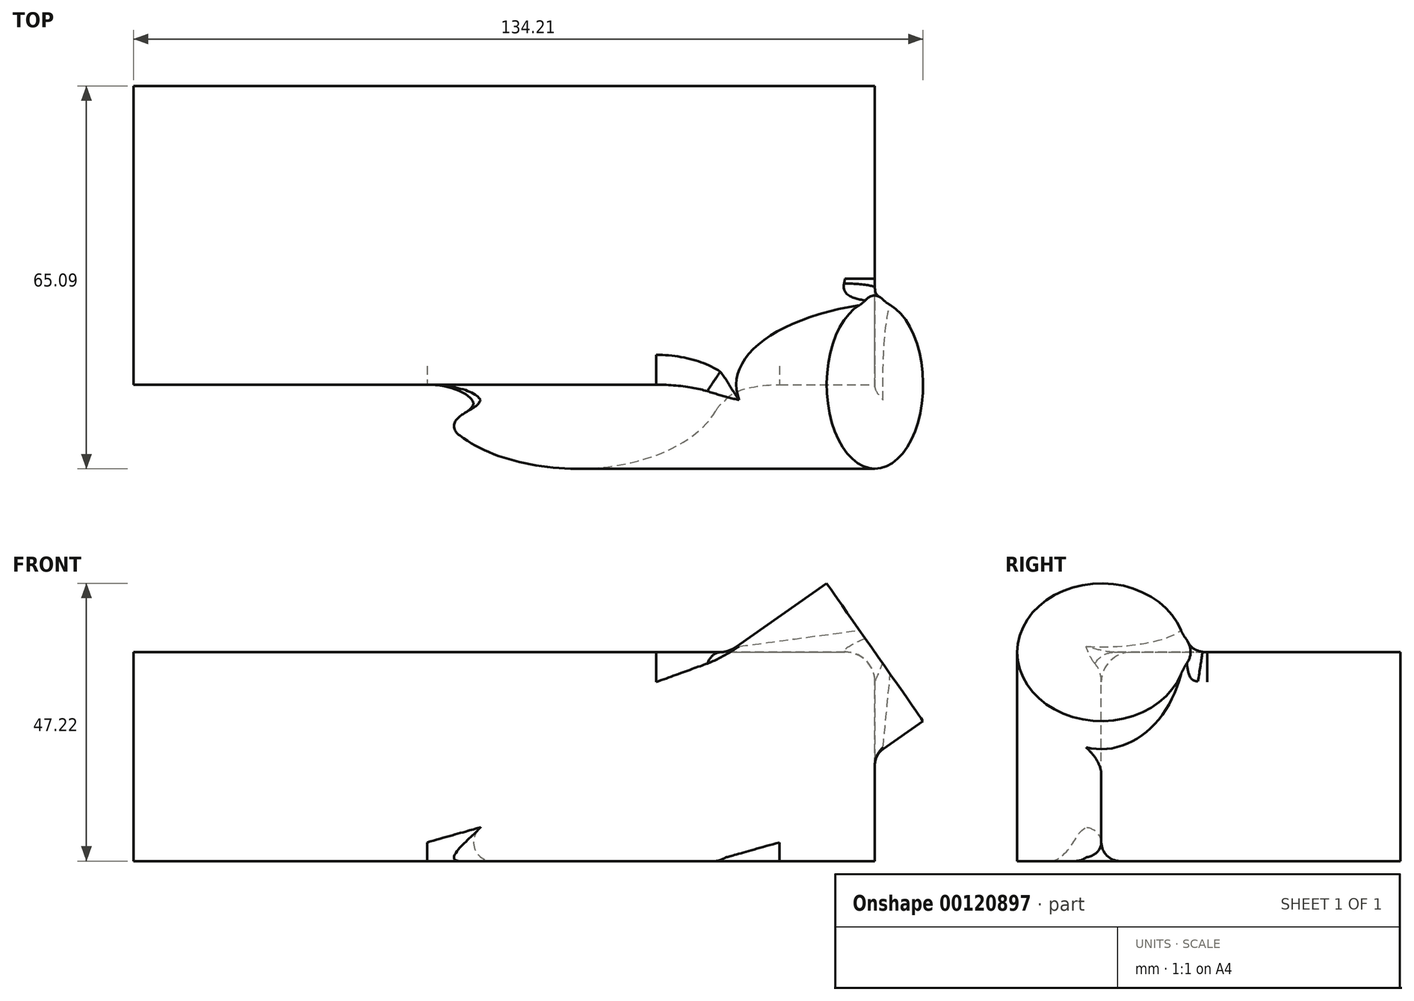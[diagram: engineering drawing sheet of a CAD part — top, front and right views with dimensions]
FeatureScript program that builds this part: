
annotation { "Feature Type Name" : "Feature", "Feature Type Description" : "" }
export const myFeature = defineFeature(function(context is Context, id is Id, definition is map)
    precondition{}
    {
        {
            var Q0;
            Q0=qCreatedBy(makeId("Front.planeOp"),FACE);
            var sketch = newSketch(context, id + "F0", { "sketchPlane" : qUnion([Q0])});
            skLineSegment(sketch, "E0.bottom", {"start": v(0, 0) * mm, "end": v(126.01, 0) * mm});
            skLineSegment(sketch, "E0.top", {"start": v(0, 35.51) * mm, "end": v(126.01, 35.51) * mm});
            skLineSegment(sketch, "E0.left", {"start": v(0, 0) * mm, "end": v(0, 35.51) * mm});
            skLineSegment(sketch, "E0.right", {"start": v(126.01, 0) * mm, "end": v(126.01, 35.51) * mm});
            skLineSegment(sketch, "E1", {"start": v(0, 0) * mm, "end": v(126.01, 35.51) * mm, "construction": true});
            skSolve(sketch);
        }
        {
            var Q0;
            Q0 = qSketchRegion(id + "F0", true);
            extrude(context, id + "F1", {"entities" : qUnion([Q0]), "endBound" : BoundingType.SYMMETRIC, "depth" : 50.8 * mm});
        }
        {
            var Q0;
            Q0=makeQuery(id+"F1.opExtrude","SWEPT_EDGE",EDGE,{"disambiguationData":[OSD([sQuery(id+"F0.wireOp",EDGE,"E0.top"),sQuery(id+"F0.wireOp",EDGE,"E0.right")])]});
            var Q1;
            Q1=makeQuery(id+"F1.opExtrude","SWEPT_FACE",FACE,{"disambiguationData":[OSD([sQuery(id+"F0.wireOp",EDGE,"E0.right")])]});
            cPlane(context, id + "F2", {"entities" : qUnion([Q0, Q1]), "cplaneType" : CPlaneType.LINE_ANGLE, "offset" : 25.4 * mm, "angle" : 325 * degree, "width" : 152.4 * mm, "height" : 152.4 * mm});
        }
        {
            var Q0;
            Q0=qCreatedBy(id+"F2.planeOp",FACE);
            var sketch = newSketch(context, id + "F3", { "sketchPlane" : qUnion([Q0])});
            skCircle(sketch, "E2", {"center": v(25.4, -43.19) * mm, "radius": 14.29 * mm});
            skSolve(sketch);
        }
        {
            var Q0;
            Q0 = qSketchRegion(id + "F3", true);
            var Q1;
            Q1=makeQuery(id+"F1.opExtrude","SWEPT_FACE",FACE,{"disambiguationData":[OSD([sQuery(id+"F0.wireOp",EDGE,"E0.bottom")])]});
            extrude(context, id + "F4", {"entities" : qUnion([Q0]), "operationType" : NewBodyOperationType.ADD, "endBound" : BoundingType.UP_TO_SURFACE, "endBoundEntityFace" : qUnion([Q1]), "depth" : 25.4 * mm});
        }
        {
            var Q0;
            Q0=makeQuery(id+"F4.boolean.opBoolean","INTERSECT",EDGE,{"disambiguationData":[OD(1.0)],"derivedFrom":[makeQuery(id+"F1.opExtrude","CAP_FACE",FACE,{"disambiguationData":[OSD([sQuery(id+"F0.wireOp",EDGE,"E0.bottom"),sQuery(id+"F0.wireOp",EDGE,"E0.top"),sQuery(id+"F0.wireOp",EDGE,"E0.left"),sQuery(id+"F0.wireOp",EDGE,"E0.right")])],"isStart":false}),makeQuery(id+"F4.opExtrude","SWEPT_FACE",FACE,{"disambiguationData":[OSD([sQuery(id+"F3.wireOp",EDGE,"E2")])]})]});
            var Q1;
            Q1=makeQuery(id+"F4.boolean.opBoolean","INTERSECT",EDGE,{"derivedFrom":[makeQuery(id+"F1.opExtrude","SWEPT_FACE",FACE,{"disambiguationData":[OSD([sQuery(id+"F0.wireOp",EDGE,"E0.right")])]}),makeQuery(id+"F4.opExtrude","SWEPT_FACE",FACE,{"disambiguationData":[OSD([sQuery(id+"F3.wireOp",EDGE,"E2")])]})]});
            var Q2;
            Q2=makeQuery(id+"F4.boolean.opBoolean","INTERSECT",EDGE,{"disambiguationData":[OD(0.0)],"derivedFrom":[makeQuery(id+"F1.opExtrude","CAP_FACE",FACE,{"disambiguationData":[OSD([sQuery(id+"F0.wireOp",EDGE,"E0.bottom"),sQuery(id+"F0.wireOp",EDGE,"E0.top"),sQuery(id+"F0.wireOp",EDGE,"E0.left"),sQuery(id+"F0.wireOp",EDGE,"E0.right")])],"isStart":false}),makeQuery(id+"F4.opExtrude","SWEPT_FACE",FACE,{"disambiguationData":[OSD([sQuery(id+"F3.wireOp",EDGE,"E2")])]})]});
            var Q3;
            {var subQ0=sQuery(id+"F0.wireOp",EDGE,"E0.bottom");var subQ1=sQuery(id+"F0.wireOp",EDGE,"E0.left");Q3=makeQuery(id+"F4.boolean.opBoolean","SPLIT",EDGE,{"disambiguationData":[TD([makeQuery(id+"F1.opExtrude","SWEPT_FACE",FACE,{"disambiguationData":[OSD([subQ1])]})])],"derivedFrom":makeQuery(id+"F1.opExtrude","CAP_EDGE",EDGE,{"disambiguationData":[OSD([subQ0])],"isStart":false})});}
            var Q4;
            {var subQ0=sQuery(id+"F0.wireOp",EDGE,"E0.bottom");var subQ1=sQuery(id+"F0.wireOp",EDGE,"E0.right");Q4=makeQuery(id+"F4.boolean.opBoolean","SPLIT",EDGE,{"disambiguationData":[TD([makeQuery(id+"F1.opExtrude","SWEPT_FACE",FACE,{"disambiguationData":[OSD([subQ1])]})])],"derivedFrom":makeQuery(id+"F1.opExtrude","CAP_EDGE",EDGE,{"disambiguationData":[OSD([subQ0])],"isStart":false})});}
            fillet(context, id + "F5", {"entities" : qUnion([Q0, Q1, Q2, Q3, Q4]), "radius" : 3.17 * mm, "tangentPropagation" : true, "allowEdgeOverflow" : false});
        }
        {
            var Q0;
            Q0=makeQuery(id+"F4.boolean.opBoolean","INTERSECT",EDGE,{"derivedFrom":[makeQuery(id+"F1.opExtrude","SWEPT_FACE",FACE,{"disambiguationData":[OSD([sQuery(id+"F0.wireOp",EDGE,"E0.top")])]}),makeQuery(id+"F4.opExtrude","SWEPT_FACE",FACE,{"disambiguationData":[OSD([sQuery(id+"F3.wireOp",EDGE,"E2")])]})]});
            fillet(context, id + "F6", {"entities" : qUnion([Q0]), "radius" : 5.08 * mm, "allowEdgeOverflow" : false});
        }
        {
            var Q0;
            {var subQ0=sQuery(id+"F3.wireOp",EDGE,"E2");var subQ1=makeQuery(id+"F4.opExtrude","SWEPT_FACE",FACE,{"disambiguationData":[OSD([subQ0])]});var subQ2=sQuery(id+"F0.wireOp",EDGE,"E0.right");var subQ3=sQuery(id+"F0.wireOp",EDGE,"E0.left");var subQ4=sQuery(id+"F0.wireOp",EDGE,"E0.top");var subQ5=sQuery(id+"F0.wireOp",EDGE,"E0.bottom");Q0=makeQuery(id+"F6.opFillet","BLEND_EDGE",EDGE,{"blendedFrom":[makeQuery(id+"F4.boolean.opBoolean","INTERSECT",EDGE,{"derivedFrom":[makeQuery(id+"F1.opExtrude","SWEPT_FACE",FACE,{"disambiguationData":[OSD([subQ4])]}),subQ1]}),makeQuery(id+"F5.opFillet","BLEND_FACE",FACE,{"disambiguationData":[OSD([subQ5,subQ4,subQ3,subQ2,subQ0]),TDD([makeQuery(id+"F4.boolean.opBoolean","INTERSECT",EDGE,{"disambiguationData":[OD(0.0)],"derivedFrom":[makeQuery(id+"F1.opExtrude","CAP_FACE",FACE,{"disambiguationData":[OSD([subQ5,subQ4,subQ3,subQ2])],"isStart":false}),subQ1]})])]})],"blendedInto":[makeQuery(id+"F5.opFillet","BLEND_FACE",FACE,{"disambiguationData":[OSD([subQ5,subQ4,subQ3,subQ2,subQ0]),TDD([makeQuery(id+"F4.boolean.opBoolean","INTERSECT",EDGE,{"disambiguationData":[OD(0.0)],"derivedFrom":[makeQuery(id+"F1.opExtrude","CAP_FACE",FACE,{"disambiguationData":[OSD([subQ5,subQ4,subQ3,subQ2])],"isStart":false}),subQ1]})])]})]});}
            var Q1;
            Q1=makeQuery(id+"F1.opExtrude","SWEPT_EDGE",EDGE,{"disambiguationData":[OSD([sQuery(id+"F0.wireOp",EDGE,"E0.top"),sQuery(id+"F0.wireOp",EDGE,"E0.right")])]});
            fillet(context, id + "F7", {"entities" : qUnion([Q0, Q1]), "radius" : 5.08 * mm, "tangentPropagation" : true, "allowEdgeOverflow" : false});
        }
    });
